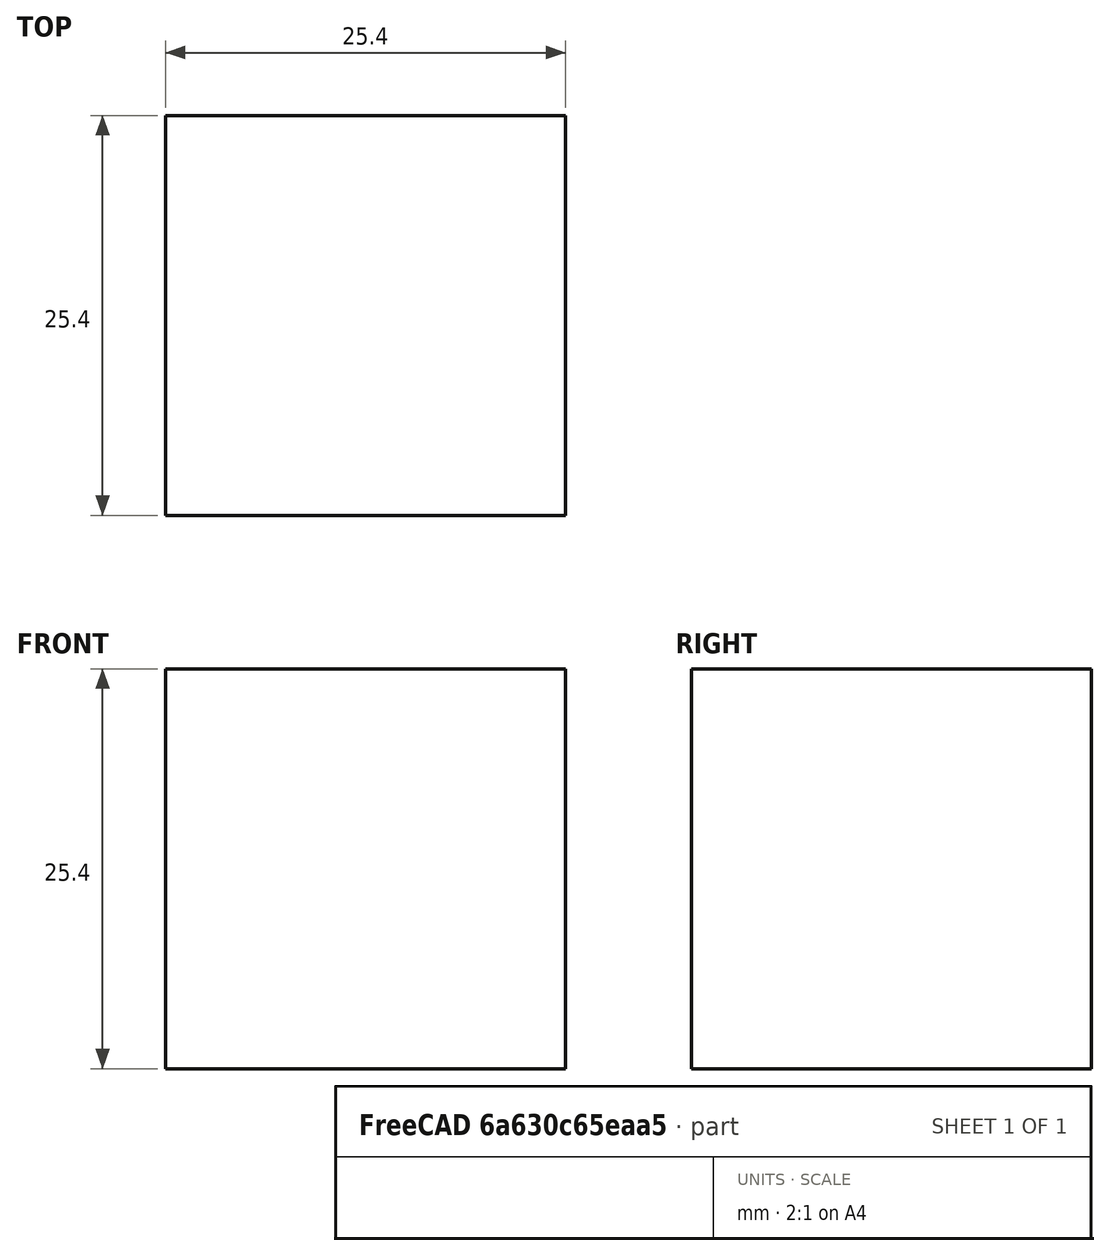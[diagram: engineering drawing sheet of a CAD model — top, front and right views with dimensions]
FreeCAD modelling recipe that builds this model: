
FCSTD DOCUMENT  (FreeCAD 1.0R38642 (Git))
Label: cube_1x1x1
Comment: A companion
License: CC0 1.0 Universal
LicenseURL: https://creativecommons.org/publicdomain/zero/1.0/
objects: Sketcher::SketchObject×1, PartDesign::Pad×1, PartDesign::Body×1
note: 6 computed .brp shape members not serialized (recipe doc carries the construction recipe); baked Part::Feature solids carry a one-line shape summary decoded from their .brp

FEATURE [Sketcher::SketchObject] Sketch  label="cube_profile"
  ArcFitTolerance = 1e-06
  AttachmentSupport = -> [XY_Plane]
  FullyConstrained = true
  MakeInternals = false
  MapMode = 5
  sketch-geometry (4):
    g0: LineSegment StartX=0 StartY=25.4 StartZ=0 EndX=0 EndY=0 EndZ=0
    g1: LineSegment StartX=0 StartY=0 StartZ=0 EndX=25.4 EndY=0 EndZ=0
    g2: LineSegment StartX=25.4 StartY=0 StartZ=0 EndX=25.4 EndY=25.4 EndZ=0
    g3: LineSegment StartX=25.4 StartY=25.4 StartZ=0 EndX=0 EndY=25.4 EndZ=0
  constraints (11):
    c: Coincident(g0,g1)
    c: Coincident(g1,g2)
    c: Coincident(g2,g3)
    c: Coincident(g3,g0)
    c: Vertical(g0)
    c: Vertical(g2)
    c: Horizontal(g1)
    c: Horizontal(g3)
    c: DistanceX(g3,g3) = 25.4
    c: DistanceY(g2,g2) = 25.4
    c: Coincident(g0,g-1)
FEATURE [PartDesign::Pad] Pad
  Direction = (0,0,1)
  Length = 25.4
  Length2 = 12.7
  Profile = -> Sketch
  ReferenceAxis = -> Sketch [N_Axis]
  Refine = true
  Suppressed = false
  Type = 0
  UseCustomVector = true
FEATURE [PartDesign::Body] Body
  AllowCompound = false
  Group = -> [Sketch,Pad]
  Origin = -> Origin
  Tip = -> Pad
